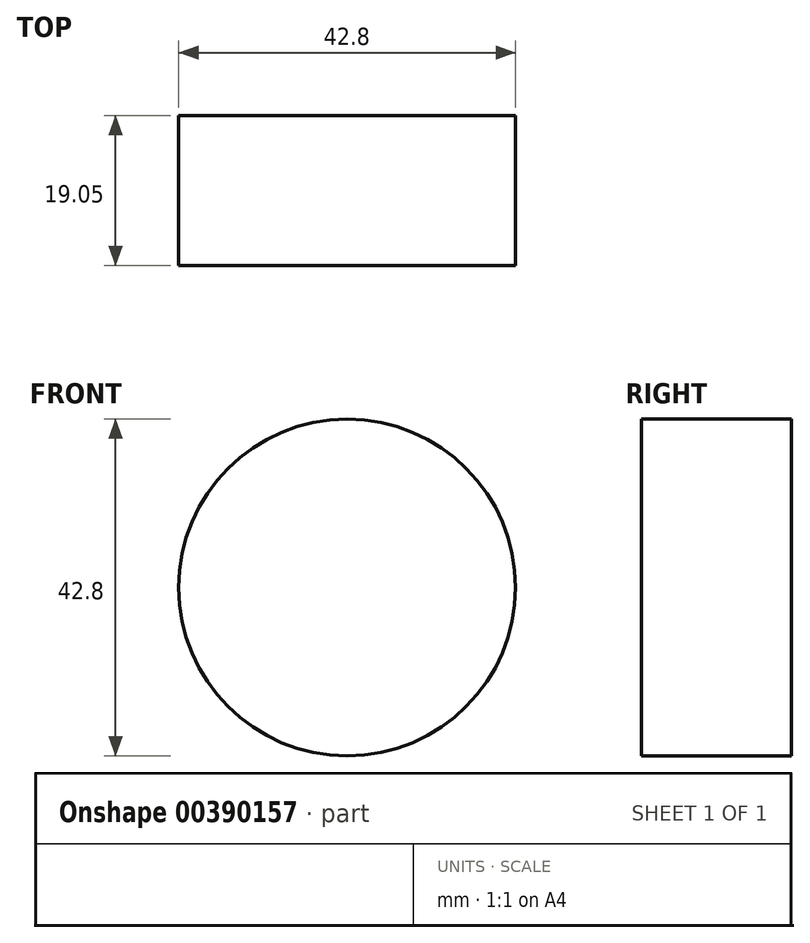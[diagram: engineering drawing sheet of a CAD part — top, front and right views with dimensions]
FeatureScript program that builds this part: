
annotation { "Feature Type Name" : "Feature", "Feature Type Description" : "" }
export const myFeature = defineFeature(function(context is Context, id is Id, definition is map)
    precondition{}
    {
        {
            var Q0;
            Q0=qCreatedBy(makeId("Front.planeOp"),FACE);
            var sketch = newSketch(context, id + "F0", { "sketchPlane" : qUnion([Q0])});
            skCircle(sketch, "E0", {"center": v(0, 0) * mm, "radius": 21.4 * mm});
            skArc(sketch, "E1", {"start": v(7.28, 20.12) * mm, "mid": v(21.83, 0.1) * mm, "end": v(25.64, 24.55) * mm});
            skArc(sketch, "E2", {"start": v(-14.47, 15.76) * mm, "mid": v(-20.83, 28.43) * mm, "end": v(-31.14, 18.7) * mm});
            skSolve(sketch);
        }
        {
            var Q0;
            Q0 = qSketchRegion(id + "F0", true);
            extrude(context, id + "F1", {"entities" : qUnion([Q0]), "depth" : 19.05 * mm});
        }
    });
